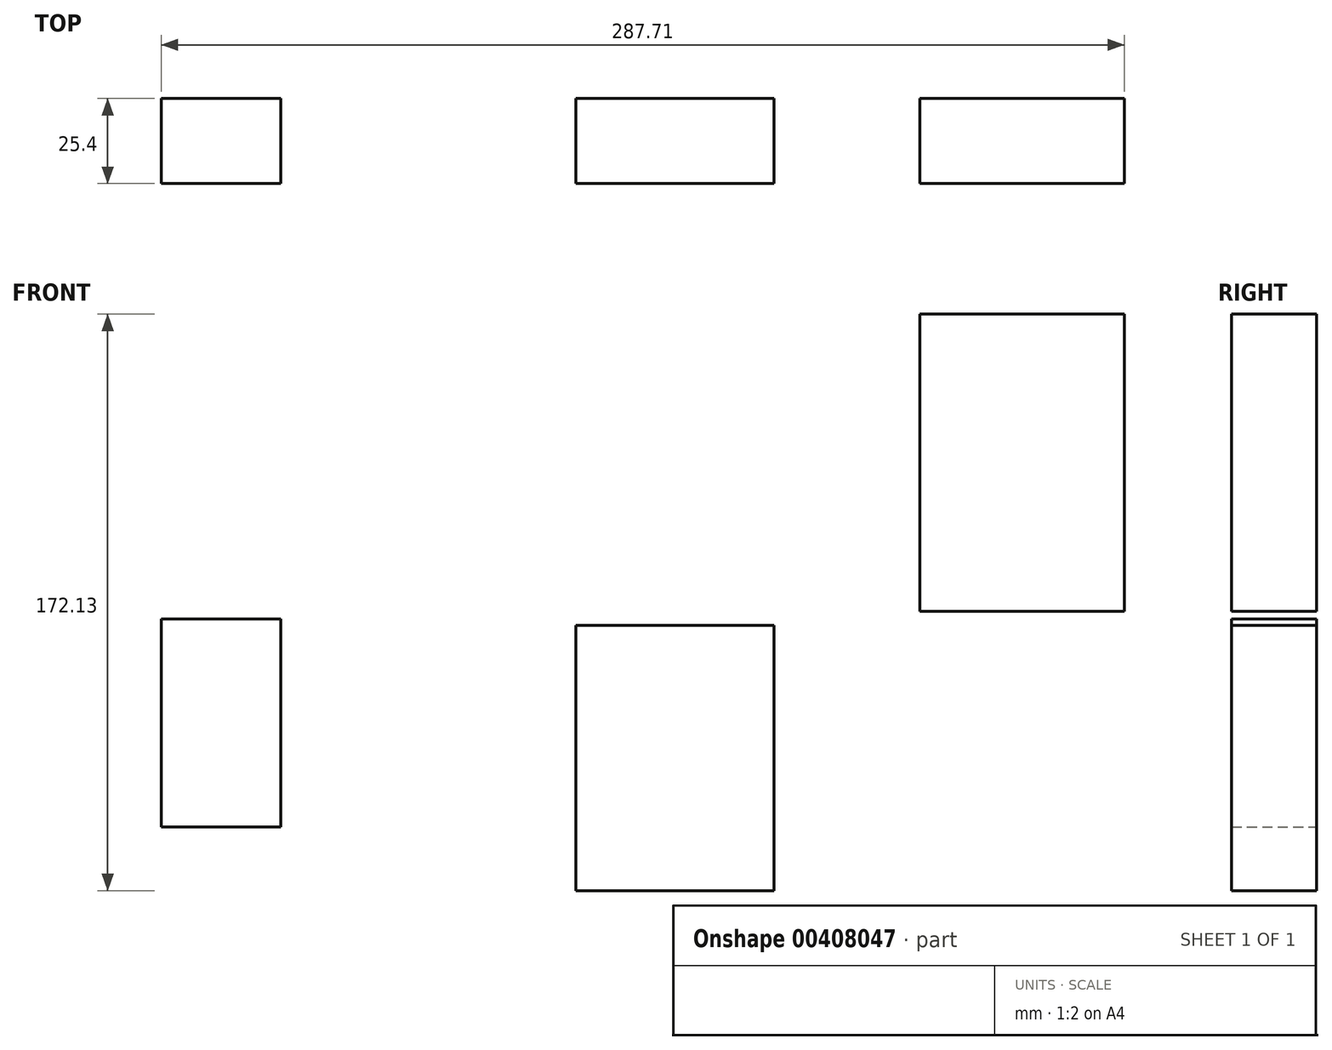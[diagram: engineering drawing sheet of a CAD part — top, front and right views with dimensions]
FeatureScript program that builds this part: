
annotation { "Feature Type Name" : "Feature", "Feature Type Description" : "" }
export const myFeature = defineFeature(function(context is Context, id is Id, definition is map)
    precondition{}
    {
        {
            var Q0;
            Q0=qCreatedBy(makeId("Front.planeOp"),FACE);
            var sketch = newSketch(context, id + "F0", { "sketchPlane" : qUnion([Q0])});
            skLineSegment(sketch, "E0.bottom", {"start": v(-82.65, 62.14) * mm, "end": v(-46.95, 62.14) * mm});
            skLineSegment(sketch, "E0.top", {"start": v(-82.65, 0) * mm, "end": v(-46.95, 0) * mm});
            skLineSegment(sketch, "E0.left", {"start": v(-82.65, 62.14) * mm, "end": v(-82.65, 0) * mm});
            skLineSegment(sketch, "E0.right", {"start": v(-46.95, 62.14) * mm, "end": v(-46.95, 0) * mm});
            skLineSegment(sketch, "E1.bottom", {"start": v(41.2, 60.28) * mm, "end": v(100.37, 60.28) * mm});
            skLineSegment(sketch, "E1.top", {"start": v(41.2, -18.94) * mm, "end": v(100.37, -18.94) * mm});
            skLineSegment(sketch, "E1.left", {"start": v(41.2, 60.28) * mm, "end": v(41.2, -18.94) * mm});
            skLineSegment(sketch, "E1.right", {"start": v(100.37, 60.28) * mm, "end": v(100.37, -18.94) * mm});
            skLineSegment(sketch, "E2.bottom", {"start": v(143.97, 153.2) * mm, "end": v(205.06, 153.2) * mm});
            skLineSegment(sketch, "E2.top", {"start": v(143.97, 64.46) * mm, "end": v(205.06, 64.46) * mm});
            skLineSegment(sketch, "E2.left", {"start": v(143.97, 153.2) * mm, "end": v(143.97, 64.46) * mm});
            skLineSegment(sketch, "E2.right", {"start": v(205.06, 153.2) * mm, "end": v(205.06, 64.46) * mm});
            skSolve(sketch);
        }
        {
            var Q0;
            Q0 = qSketchRegion(id + "F0", true);
            extrude(context, id + "F1", {"entities" : qUnion([Q0]), "depth" : 25.4 * mm});
        }
    });
